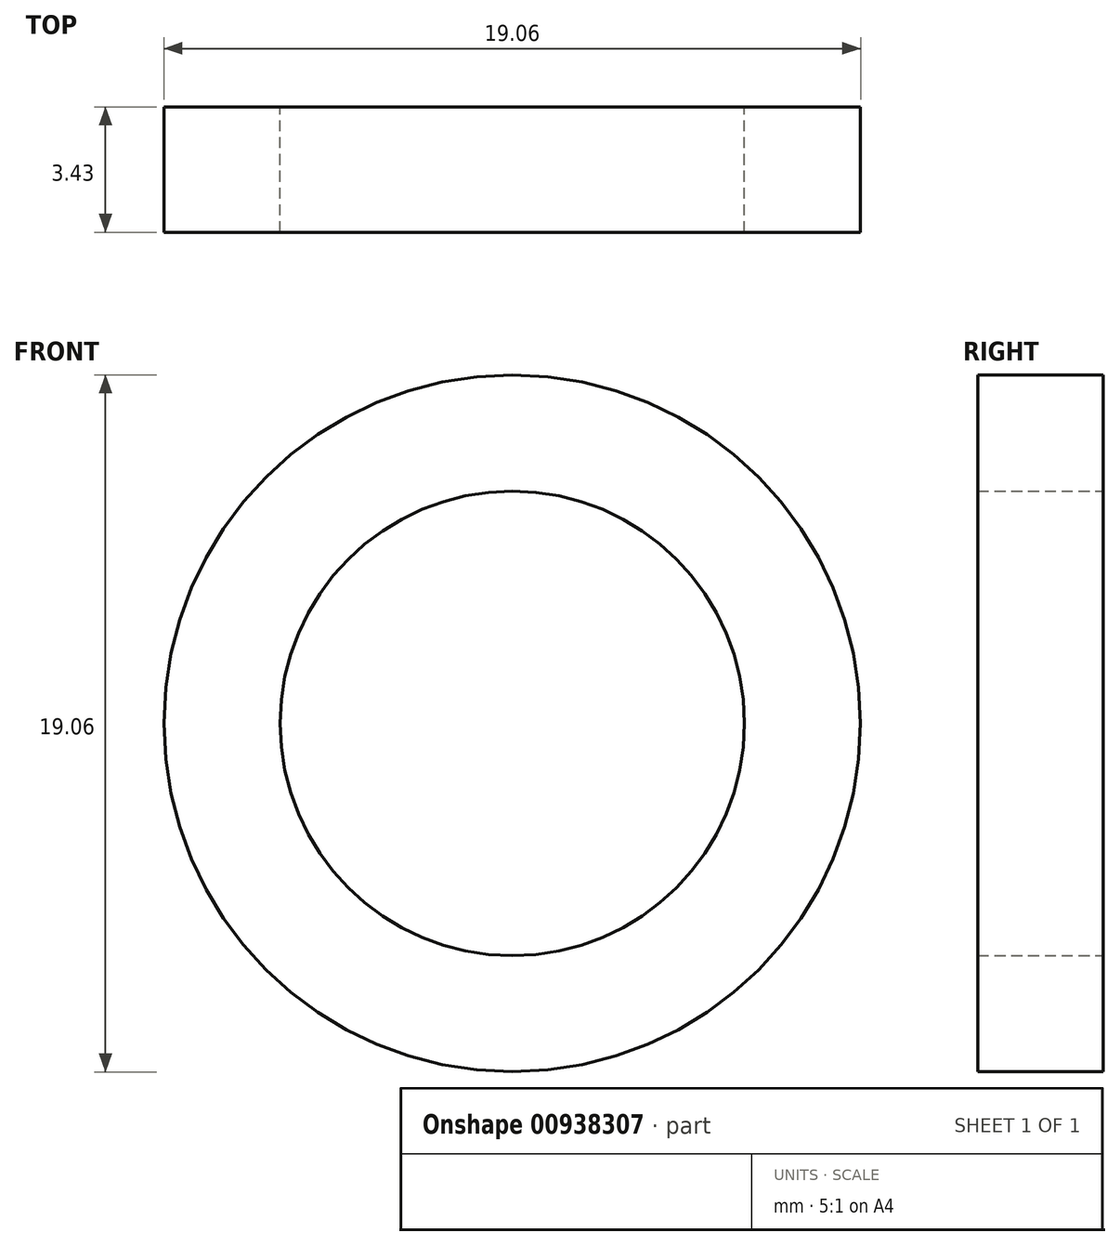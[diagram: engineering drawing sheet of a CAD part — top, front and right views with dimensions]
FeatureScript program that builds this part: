
annotation { "Feature Type Name" : "Feature", "Feature Type Description" : "" }
export const myFeature = defineFeature(function(context is Context, id is Id, definition is map)
    precondition{}
    {
        {
            var Q0;
            Q0=qCreatedBy(makeId("Front.planeOp"),FACE);
            var sketch = newSketch(context, id + "F0", { "sketchPlane" : qUnion([Q0])});
            skCircle(sketch, "E0", {"center": v(0, 0) * mm, "radius": 6.35 * mm});
            skCircle(sketch, "E1", {"center": v(0, 0) * mm, "radius": 9.53 * mm});
            skSolve(sketch);
        }
        {
            var Q0;
            Q0=makeQuery(id+"F0.imprint","IMPRINT",FACE,{"disambiguationData":[TD([[makeQuery(id+"F0.imprint","IMPRINT",EDGE,{"derivedFrom":sQuery(id+"F0.wireOp",EDGE,"E0")}),-1.0]])]});
            extrude(context, id + "F1", {"entities" : qUnion([Q0]), "depth" : 3.43 * mm, "offsetDistance" : 25.4 * mm});
        }
    });
